# Revit family: QF_BPRO_SAW L-2_572156
name_source: partatom
category: Sonderausstattung
revit_build: Autodesk Revit 2018 (Build: 20190510_1515(x64)
units: mm (PartAtom-declared; Revit-internal decimal feet)

## family parameters
Arbeitsebenenbasiert = Nein
Beim Laden mit Abzugskörper schneiden = Nein
Bemaßung runder Anschluss = Durchmesser verwenden
Gemeinsam genutzt = Nein
Immer vertikal = Ja
Raumberechnungspunkt = Ja
Teiletyp = Normal

## types (1)
- SAW L-2
    3fach = Nein
    Artikel Nummer = 572156
    Beckenlänge = 305 mm
    Beckentiefe = 200 mm  [stored 0.656168 ft]
    Beschreibung = Speisenausgabewagen;
speziell für den Einsatz an einer Anfahrwand (Schiebegriff und Bedienelemente an der Längsseite);
2 Einzelbecken für 2x GN 1/1-200 oder deren Unterteilung;
mit Temperaturregler
    Beschreibung durch Hersteller analog Leistungsverzeichniskurztext = Abmessungen

Länge:					900 mm
Breite:					749 mm 
Höhe:					933 mm


Ausführung

Aufbau
Der Speisenausgabewagen besteht komplett aus CNS 18/10. Die Oberfläche ist mikroliert. Die fugenlos eingeschweißten, tiefgezogenen Warmhaltebecken sind nass oder trocken getrennt voneinander beheiz- und regelbar. In die einzelnen Becken ist eine Markierung geprägt, welche der Füllmenge von 4 Litern entspricht. Um die Becken läuft ein Profilrand. Die Nummerierung der Becken ist in die Abdeckung geprägt. Die Becken sind an der Unterseite mit einem, gegen unbeabsichtigtes öffnen gesicherten, Ablasshahn ausgestattet.
Dieser Speisenausgabewagen ist speziell für den Einsatz an einer Anfahrwand konzipiert.
Das Bedienfeld liegt mit Ein/Aus-Schalter, Kontrollleuchte, Spiralkabel, Blindsteckerbuchse und Temperaturregler an der Längsseite. Der Temperaturregler sichert die stufenlose Temperatureinstellung je Becken. 
Längsseitig ist ein CNS-Sicherheits-Schiebegriff mit seitlichen Stoßschutzelementen aus Kunststoff (Polyamid) angebracht. 
Das offene Untergestell besitzt vier stabile Vierkantrohre, dazwischen eingeschweißt ein abgekantetes Ablagebord.
Fahrbar ist der Wagen mittels rostfreien Kunststoffrollen (4 Lenkrollen, davon 2 mit Feststeller mit 125 mm ø). Massive Stoßecken aus Kunststoff (Polyamid) an allen vier Ecken schützen vor Beschädigung.

Zubehör/ Optionen

•	Hustenschutz aus ESG-Sicherheitsglas kundenseitig bis zur Abdeckung heruntergeführt oder kundenseitig mit einer Durchreichehöhe von 275 mm.
Optional mit Wärmebord aus CNS 
(2 Keramikwärmestrahler à 250 W, 230 V, ungeregelt, gemeinsam mit dem jeweiligen Bain-Marie-Becken geschaltet.)
Länge Glasbord: 700 mm
Höhe inkl. Aufsatz: ca. 1325 mm
•	GN-Deckel-Ablage, zur Aufnahme von GN-Deckel 1/1 und deren Unterteilung, stirnseitig angebracht
•	weitere Rollenausführungen siehe Gesamt-Preisliste
•	Arbeitshöhe (Oberkante Abdeckung) von 700 mm bis 899 mm konfigurierbar (Standard: 900 mm)




Technische Daten

Werkstoff:		CNS 18/10
Gewicht:		35,5 kg 
Kapazität:		2 Warmhaltebecken
Warmhaltebecken:	für GN 1/1-200 oder deren Unterteilung
		Temperatur von +30°C bis +95 °C regelbar 
Anschlusswert:		220-240V / 50Hz / 1,4 kW


Besonderheit

•	Spritz- und strahlwassergeschützt (IPX 5)
•	Abdeckung mit Profilrand
•	die Becken sind nass oder trocken beheizbar
•	die Becken können einzeln beheizt und geregelt werden
•	Ablasshahn gegen unbeabsichtigtes Öffnen gesichert
•	geeignet für Optimierungsanlagen
•	Bedienelemente und Schiebegriff befinden sich an der Längsseite
•	gemäß DIN 18867, Teil 7



Fabrikat

Hersteller:			B.PRO
Modell:				SAW L-2
				B.PRO
    Beschreibung durch Hersteller analog Leistungsverzeichnislangtext = Abmessungen

Länge:					900 mm
Breite:					749 mm 
Höhe:					933 mm


Ausführung

Aufbau
Der Speisenausgabewagen besteht komplett aus CNS 18/10. Die Oberfläche ist mikroliert. Die fugenlos eingeschweißten, tiefgezogenen Warmhaltebecken sind nass oder trocken getrennt voneinander beheiz- und regelbar. In die einzelnen Becken ist eine Markierung geprägt, welche der Füllmenge von 4 Litern entspricht. Um die Becken läuft ein Profilrand. Die Nummerierung der Becken ist in die Abdeckung geprägt. Die Becken sind an der Unterseite mit einem, gegen unbeabsichtigtes öffnen gesicherten, Ablasshahn ausgestattet.
Dieser Speisenausgabewagen ist speziell für den Einsatz an einer Anfahrwand konzipiert.
Das Bedienfeld liegt mit Ein/Aus-Schalter, Kontrollleuchte, Spiralkabel, Blindsteckerbuchse und Temperaturregler an der Längsseite. Der Temperaturregler sichert die stufenlose Temperatureinstellung je Becken. 
Längsseitig ist ein CNS-Sicherheits-Schiebegriff mit seitlichen Stoßschutzelementen aus Kunststoff (Polyamid) angebracht. 
Das offene Untergestell besitzt vier stabile Vierkantrohre, dazwischen eingeschweißt ein abgekantetes Ablagebord.
Fahrbar ist der Wagen mittels rostfreien Kunststoffrollen (4 Lenkrollen, davon 2 mit Feststeller mit 125 mm ø). Massive Stoßecken aus Kunststoff (Polyamid) an allen vier Ecken schützen vor Beschädigung.

Zubehör/ Optionen

•	Hustenschutz aus ESG-Sicherheitsglas kundenseitig bis zur Abdeckung heruntergeführt oder kundenseitig mit einer Durchreichehöhe von 275 mm.
Optional mit Wärmebord aus CNS 
(2 Keramikwärmestrahler à 250 W, 230 V, ungeregelt, gemeinsam mit dem jeweiligen Bain-Marie-Becken geschaltet.)
Länge Glasbord: 700 mm
Höhe inkl. Aufsatz: ca. 1325 mm
•	GN-Deckel-Ablage, zur Aufnahme von GN-Deckel 1/1 und deren Unterteilung, stirnseitig angebracht
•	weitere Rollenausführungen siehe Gesamt-Preisliste
•	Arbeitshöhe (Oberkante Abdeckung) von 700 mm bis 899 mm konfigurierbar (Standard: 900 mm)




Technische Daten

Werkstoff:		CNS 18/10
Gewicht:		35,5 kg 
Kapazität:		2 Warmhaltebecken
Warmhaltebecken:	für GN 1/1-200 oder deren Unterteilung
		Temperatur von +30°C bis +95 °C regelbar 
Anschlusswert:		220-240V / 50Hz / 1,4 kW


Besonderheit

•	Spritz- und strahlwassergeschützt (IPX 5)
•	Abdeckung mit Profilrand
•	die Becken sind nass oder trocken beheizbar
•	die Becken können einzeln beheizt und geregelt werden
•	Ablasshahn gegen unbeabsichtigtes Öffnen gesichert
•	geeignet für Optimierungsanlagen
•	Bedienelemente und Schiebegriff befinden sich an der Längsseite
•	gemäß DIN 18867, Teil 7



Fabrikat

Hersteller:			B.PRO
Modell:				SAW L-2
				B.PRO
    Elektrische leistung = 1400 W
    Frequenz = 50 Hz
    Gerätegewicht Netto = 35.50 kg
    Großküchengerätezuordnung = Ja
    Hauptschalter integriert = Ja
    Hersteller = B.PRO GmbH
    Höhe = 933 mm  [stored 3.06102 ft]
    Höhe Arbeitsebene = 900 mm  [stored 2.95276 ft]
    Internetadresse Gerätehersteller = https://www.bpro-solutions.com
    Internetadresse für Ersatzteilliste = https://www.bpro-solutions.com
    Kosten = 1592.5 $
    Länge Gerätebreite = 894 mm
    Länge Korpus = 816 mm
    Material = QF_Metal-Stainless-Steel_general
    Material Dichtung = QF_Rubber-Black-Matt
    Material Kabel = QF_Rubber-Black-Matt
    Material Knöpfe1 = QF_Plastic-Black-Glossy
    Material Kunststoffteile = QF_Plastic-Black-Matt
    Material Metall glänzend = QF_Metal-Stainless-Steel_glossy
    Material Stoßschutz = QF_Rubber-Black-Matt
    Mittelabstand Schalter Strg = 46 mm  [stored 0.150919 ft]
    Modell = SAW L-2
    Schalldruckpegel = < 70 dB(A)
    Sockelhöhe = 168 mm  [stored 0.551181 ft]
    Spannung = 220 V
    Stecker System = Schuko Stecker
    Tiefe = 746 mm
    Tiefe Korpus = 630 mm
    Typenkommentare = Speisenausgabewagen, 2 Becken, 2 Schränke
    URL = https://www.bpro-solutions.com
    Versatz Becken Mitte Strg = 220 mm
    Warnhinweise = Wenn das Gerät nicht für die vorliegende Netzspannung oder Netzfrequenz ausgelegt ist, kann die Geräteelektrik zerstört werden. Vor dem Anschließen sicherstellen, dass die auf dem Typenschild angegebene Netzspannung und Netzfrequenz mit den entsprechenden Werten der Netzsteckdose übereinstimmen.

Spannungsrisse durch kaltes Wasser in heißen Bain-Marie-Becken. Wenn in heiße Bain-Marie-Becken kaltes Wasser gefüllt wird, kann der rasche Temperaturwechsel Spannungsrisse verursachen, die zu Korrosion führen können. Vor dem Befüllen mit kaltem Wasser Bain-Marie-Becken abkühlen lassen oder heiße Bain-Marie-Becken mit heißem Wasser befüllen.

Eingeklemmter Fuß. Beim Lösen und Arretieren der Feststellbremse kann der Fuß eingeklemmt und dabei verletzt werden. Darauf achten, dass der Fuß nicht zwischen die Feststellbremse und die Stoßecke gerät.

Heiße Bain-Marie-Becken / Heiße Geräteflächn / Heiße Gastronormbehälter. Im Warmhaltebetrieb können Gerätebecken, Geräteflächen und darin enthaltene Gastronormbehälter oder andere Gegenstände heiß werden und Verbrennungen verursachen. Heiße Teile nur geschützt (z.B. mit Topflappen oder Schutzhandschuhe) anfassen.

Heiße flüssige Speisen. Heiße flüssige Speisen können über den Rand des Gastronormbehälters fließen und Verbrühungen verursachen. Gastronormbehälter waagerecht halten. Gastronormbehälter stets mit Dichtungsdeckeln verschließen.

Heißes Wasser. Bei Nassbeschickung befindet sich im Bain-Marie-Becken nach Gebrauch heißes Wasser. Wenn das heiße Wasser abgelassen wird, besteht die Gefahr von Verbrühungen. Gerät vor Reinigung abkühlen lassen.

Ausführliche Gefahrenhinweise entnehmen Sie der Betriebsanleitung.
    Zubehör = Nein
    Zuleitung zum Gerät im Lieferumfang = Ja

note: [stored X ft] marks values corroborated as IEEE doubles in the binary element streams (Revit-internal decimal feet)
